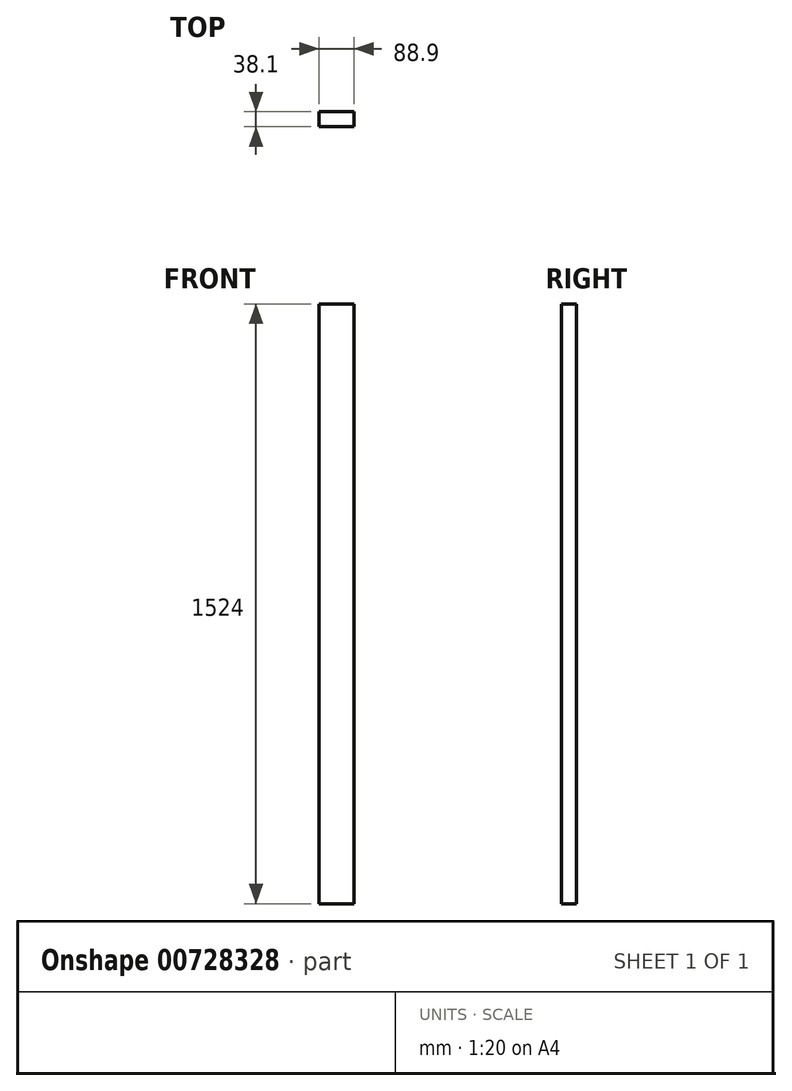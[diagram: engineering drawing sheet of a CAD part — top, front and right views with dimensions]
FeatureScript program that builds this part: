
annotation { "Feature Type Name" : "Feature", "Feature Type Description" : "" }
export const myFeature = defineFeature(function(context is Context, id is Id, definition is map)
    precondition{}
    {
        {
            var Q0;
            Q0=qCreatedBy(makeId("Front.planeOp"),FACE);
            var sketch = newSketch(context, id + "F0", { "sketchPlane" : qUnion([Q0])});
            skLineSegment(sketch, "E0.bottom", {"start": v(44.45, -762) * mm, "end": v(-44.45, -762) * mm});
            skLineSegment(sketch, "E0.top", {"start": v(44.45, 762) * mm, "end": v(-44.45, 762) * mm});
            skLineSegment(sketch, "E0.left", {"start": v(44.45, -762) * mm, "end": v(44.45, 762) * mm});
            skLineSegment(sketch, "E0.right", {"start": v(-44.45, -762) * mm, "end": v(-44.45, 762) * mm});
            skPoint(sketch, "E0.middle", {"position": v(0, 0) * mm});
            skSolve(sketch);
        }
        {
            var Q0;
            Q0=qSketchRegion(id+"F0",true);
            extrude(context, id + "F1", {"entities" : qUnion([Q0]), "depth" : 38.1 * mm, "offsetDistance" : 25.4 * mm});
        }
    });
